# Revit family: Drain_Trench_Zurn-Z886-PVS
name_source: partatom
category: Plumbing Fixtures
units: mm (PartAtom-declared; Revit-internal decimal feet)

## family parameters
Always vertical = Yes
Cut with Voids When Loaded = No
Maintain Annotation Orientation = No
OmniClass Number = 23.70.50.21.24.14
OmniClass Title = Deck Waste Water Drains
Part Type = Normal
Room Calculation Point = No
Round Connector Dimension = Use Radius
Shared = No
Work Plane-Based = No

## types (1)
- Load Family Type Catalog
    Assembly Code = D2030300
    Bottom Outlet = Yes
    CW Connection = No
    CWFU = 0
    Connector Radius = 2 "
    Deep = 6.85 "
    Default Elevation = 20 "
    Description = 3/8 [10] WIDE REVEAL TRENCH DRAIN SYSTEM W/ PAVER SLOT GRATE
    End Outlet = No
    End to Center of Bottom Outlet = 3 "
    Flow = 93 GPM
    Grate Material = Iron - Zurn - Cast - Ductile - Painted Black
    HW Connection = No
    HWFU = 0
    Inner Diameter = 4.026 "
    Main Material = Polymer - Zurn - HDPE - Grey
    Manufacturer = Zurn Industries, LLC
    Model = Z886-PVS
    Modified Date = 03/26/26
    Nominal  Diameter = 4 "
    Outlet Bottom OD = 2.375 "
    Outlet Depth = 2 "
    Outlet Visiblity = No
    Outter Diameter = 4.5 "
    Pipe Connection Deep End = 3 "
    Pipe Connection Shallow End = 3 "
    Product Documentation Link = https://files.zurn.com
    Product Page URL = https://www.zurn.com
    Product data url = https://www.bimobject.com
    Shallow = 6.25 "
    Type Comments = Z886-PVS-8601 W/-E2 x 6.25x 6.85 With 2 Inch No-Hub End outlet
    URL = http://www.zurn.com
    Vent Connection = No
    WFU = 1
    Waste Connection = Yes

## geometry (parser evidence)
native form markers: Blend x4, Sweep x2
no freeform markers — native parametric forms only
